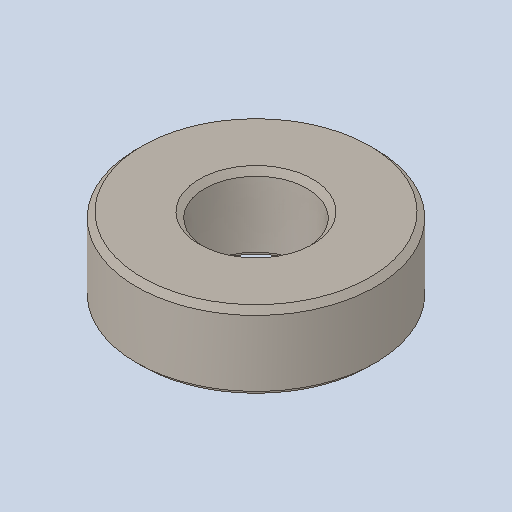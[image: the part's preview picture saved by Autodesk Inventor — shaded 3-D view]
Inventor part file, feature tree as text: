
AUTODESK INVENTOR PART (.ipt)
format: ipt  version: 2023 (Build 270158000, 158)  size: 102,912 bytes
history: native  units: in
note: dims shown in document units (in); Inventor stores cm internally (conversion verified against a paired STEP export)
features: chamfer x1
ambient origin geometry x8: Origin, YZ Plane, XZ Plane, XY Plane, X Axis, Y Axis, Z Axis, Center Point
bodies: Solid1 (feature_tree)
feature tree (1):
  chamfer  "Chamfer1"  [1 undecoded]
note: 1 required parameter value undecoded (feature->parameter linkage not recoverable at this tier; creation-order binding heuristic only, values carry confidence <= 0.55)
